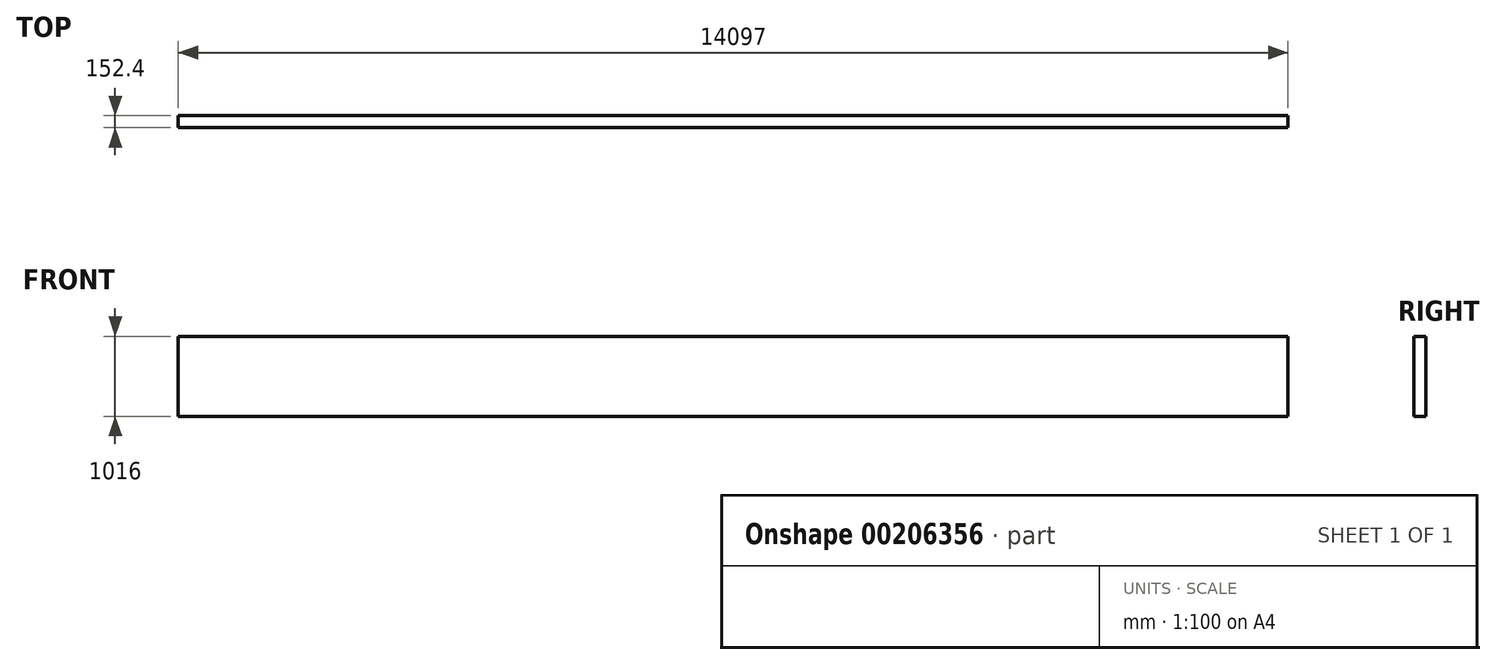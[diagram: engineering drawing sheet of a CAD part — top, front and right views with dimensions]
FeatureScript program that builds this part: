
annotation { "Feature Type Name" : "Feature", "Feature Type Description" : "" }
export const myFeature = defineFeature(function(context is Context, id is Id, definition is map)
    precondition{}
    {
        {
            var Q0;
            Q0=qCreatedBy(makeId("Front.planeOp"),FACE);
            var sketch = newSketch(context, id + "F0", { "sketchPlane" : qUnion([Q0])});
            skLineSegment(sketch, "E0.bottom", {"start": v(6723.68, -508) * mm, "end": v(-7373.32, -508) * mm});
            skLineSegment(sketch, "E0.top", {"start": v(6723.68, 508) * mm, "end": v(-7373.32, 508) * mm});
            skLineSegment(sketch, "E0.left", {"start": v(6723.68, -508) * mm, "end": v(6723.68, 508) * mm});
            skLineSegment(sketch, "E0.right", {"start": v(-7373.32, -508) * mm, "end": v(-7373.32, 508) * mm});
            skPoint(sketch, "E0.middle", {"position": v(-324.82, 0) * mm});
            skSolve(sketch);
        }
        {
            var Q0;
            Q0=makeQuery(id+"F0.imprint","IMPRINT",FACE,{"disambiguationData":[TD([[makeQuery(id+"F0.imprint","IMPRINT",EDGE,{"derivedFrom":sQuery(id+"F0.wireOp",EDGE,"E0.bottom")}),-1.0]])]});
            extrude(context, id + "F1", {"entities" : qUnion([Q0]), "oppositeDirection" : true, "depth" : 152.4 * mm});
        }
    });
